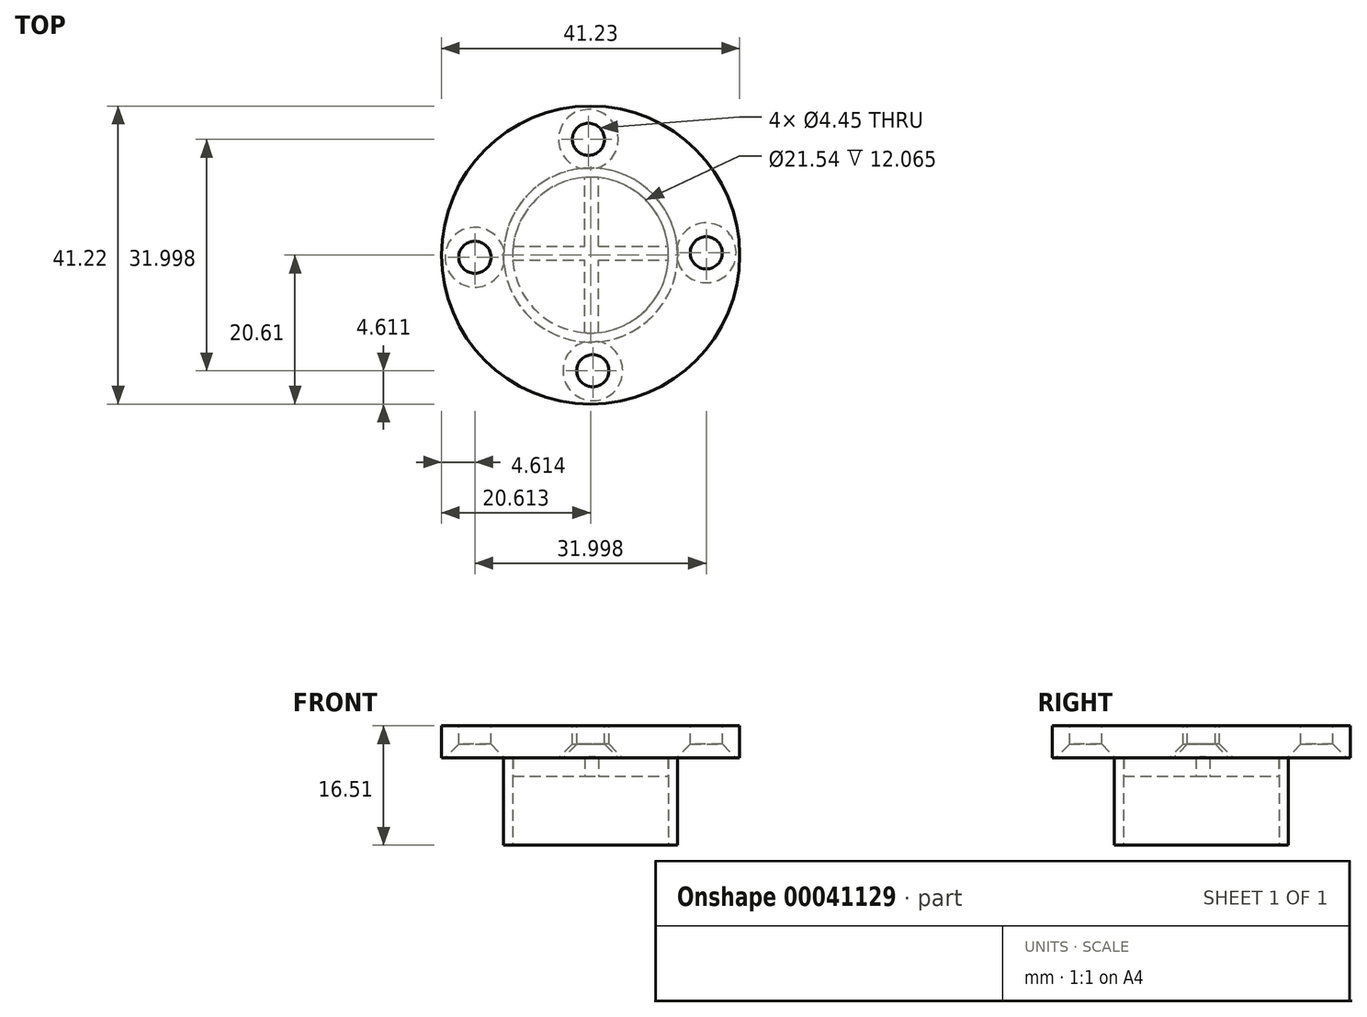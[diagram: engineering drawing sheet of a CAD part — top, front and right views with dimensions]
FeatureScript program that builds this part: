
annotation { "Feature Type Name" : "Feature", "Feature Type Description" : "" }
export const myFeature = defineFeature(function(context is Context, id is Id, definition is map)
    precondition{}
    {
        {
            var Q0;
            Q0=qCreatedBy(makeId("Top.planeOp"),FACE);
            var sketch = newSketch(context, id + "F0", { "sketchPlane" : qUnion([Q0])});
            skCircle(sketch, "E0", {"center": v(-31.53, -46.9) * mm, "radius": 12.04 * mm});
            skCircle(sketch, "E1", {"center": v(-31.53, -46.9) * mm, "radius": 10.77 * mm});
            skSolve(sketch);
        }
        {
            var Q0;
            Q0=makeQuery(id+"F0.imprint","IMPRINT",FACE,{"disambiguationData":[TD([[makeQuery(id+"F0.imprint","IMPRINT",EDGE,{"derivedFrom":sQuery(id+"F0.wireOp",EDGE,"E0")}),1.0]])]});
            extrude(context, id + "F1", {"entities" : qUnion([Q0]), "depth" : 12.06 * mm});
        }
        {
            var Q0;
            Q0=makeQuery(id+"F1.opExtrude","CAP_FACE",FACE,{"disambiguationData":[OSD([sQuery(id+"F0.wireOp",EDGE,"E0"),sQuery(id+"F0.wireOp",EDGE,"E1")])],"isStart":false});
            var sketch = newSketch(context, id + "F2", { "sketchPlane" : qUnion([Q0])});
            skCircle(sketch, "E2", {"center": v(-31.53, -46.9) * mm, "radius": 20.61 * mm});
            skSolve(sketch);
        }
        {
            var Q0;
            Q0 = qSketchRegion(id + "F2", true);
            extrude(context, id + "F3", {"entities" : qUnion([Q0]), "operationType" : NewBodyOperationType.ADD, "depth" : 4.44 * mm});
        }
        {
            var Q0;
            Q0=makeQuery(id+"F3.opExtrude","CAP_FACE",FACE,{"disambiguationData":[OSD([sQuery(id+"F2.wireOp",EDGE,"E2")])],"isStart":false});
            var sketch = newSketch(context, id + "F4", { "sketchPlane" : qUnion([Q0])});
            skCircle(sketch, "E3", {"center": v(-31.83, -30.9) * mm, "radius": 2.22 * mm});
            skPoint(sketch, "E4", {"position": v(-31.53, -46.9) * mm});
            skLineSegment(sketch, "E5", {"start": v(-31.53, -46.9) * mm, "end": v(-31.83, -30.9) * mm});
            skCircle(sketch, "E6", {"center": v(-31.22, -62.89) * mm, "radius": 2.23 * mm});
            skLineSegment(sketch, "E7", {"start": v(-31.53, -46.9) * mm, "end": v(-31.22, -62.89) * mm});
            skCircle(sketch, "E8", {"center": v(-47.53, -47.2) * mm, "radius": 2.23 * mm});
            skCircle(sketch, "E9", {"center": v(-15.53, -46.59) * mm, "radius": 2.23 * mm});
            skLineSegment(sketch, "E10", {"start": v(-31.53, -46.9) * mm, "end": v(-47.53, -47.2) * mm});
            skLineSegment(sketch, "E11", {"start": v(-31.53, -46.9) * mm, "end": v(-15.53, -46.59) * mm});
            skSolve(sketch);
        }
        {
            var Q0;
            Q0 = qSketchRegion(id + "F4", true);
            extrude(context, id + "F5", {"entities" : qUnion([Q0]), "operationType" : NewBodyOperationType.REMOVE, "endBound" : BoundingType.THROUGH_ALL, "oppositeDirection" : true, "depth" : 25.4 * mm});
        }
        {
            var Q0;
            {var subQ0=sQuery(id+"F2.wireOp",EDGE,"E2");Q0=makeQuery(id+"F5.boolean.opBoolean","INTERSECT",EDGE,{"derivedFrom":[makeQuery(id+"F3.boolean.opBoolean","SPLIT",FACE,{"disambiguationData":[TD([makeQuery(id+"F1.opExtrude","SWEPT_FACE",FACE,{"disambiguationData":[OSD([sQuery(id+"F0.wireOp",EDGE,"E0")])]})])],"derivedFrom":makeQuery(id+"F3.opExtrude","CAP_FACE",FACE,{"disambiguationData":[OSD([subQ0])],"isStart":true})}),makeQuery(id+"F5.opExtrude","SWEPT_FACE",FACE,{"disambiguationData":[OSD([sQuery(id+"F4.wireOp",EDGE,"E6")])]})]});}
            var Q1;
            {var subQ0=sQuery(id+"F2.wireOp",EDGE,"E2");Q1=makeQuery(id+"F5.boolean.opBoolean","INTERSECT",EDGE,{"derivedFrom":[makeQuery(id+"F3.boolean.opBoolean","SPLIT",FACE,{"disambiguationData":[TD([makeQuery(id+"F1.opExtrude","SWEPT_FACE",FACE,{"disambiguationData":[OSD([sQuery(id+"F0.wireOp",EDGE,"E0")])]})])],"derivedFrom":makeQuery(id+"F3.opExtrude","CAP_FACE",FACE,{"disambiguationData":[OSD([subQ0])],"isStart":true})}),makeQuery(id+"F5.opExtrude","SWEPT_FACE",FACE,{"disambiguationData":[OSD([sQuery(id+"F4.wireOp",EDGE,"E9")])]})]});}
            var Q2;
            {var subQ0=sQuery(id+"F2.wireOp",EDGE,"E2");Q2=makeQuery(id+"F5.boolean.opBoolean","INTERSECT",EDGE,{"derivedFrom":[makeQuery(id+"F3.boolean.opBoolean","SPLIT",FACE,{"disambiguationData":[TD([makeQuery(id+"F1.opExtrude","SWEPT_FACE",FACE,{"disambiguationData":[OSD([sQuery(id+"F0.wireOp",EDGE,"E0")])]})])],"derivedFrom":makeQuery(id+"F3.opExtrude","CAP_FACE",FACE,{"disambiguationData":[OSD([subQ0])],"isStart":true})}),makeQuery(id+"F5.opExtrude","SWEPT_FACE",FACE,{"disambiguationData":[OSD([sQuery(id+"F4.wireOp",EDGE,"E8")])]})]});}
            var Q3;
            {var subQ0=sQuery(id+"F2.wireOp",EDGE,"E2");Q3=makeQuery(id+"F5.boolean.opBoolean","INTERSECT",EDGE,{"derivedFrom":[makeQuery(id+"F3.boolean.opBoolean","SPLIT",FACE,{"disambiguationData":[TD([makeQuery(id+"F1.opExtrude","SWEPT_FACE",FACE,{"disambiguationData":[OSD([sQuery(id+"F0.wireOp",EDGE,"E0")])]})])],"derivedFrom":makeQuery(id+"F3.opExtrude","CAP_FACE",FACE,{"disambiguationData":[OSD([subQ0])],"isStart":true})}),makeQuery(id+"F5.opExtrude","SWEPT_FACE",FACE,{"disambiguationData":[OSD([sQuery(id+"F4.wireOp",EDGE,"E3")])]})]});}
            chamfer(context, id + "F6", {"entities" : qUnion([Q0, Q1, Q2, Q3]), "width" : 1.9 * mm, "tangentPropagation" : true});
        }
        {
            var Q0;
            {var subQ0=sQuery(id+"F2.wireOp",EDGE,"E2");Q0=makeQuery(id+"F3.boolean.opBoolean","SPLIT",FACE,{"disambiguationData":[TD([makeQuery(id+"F1.opExtrude","SWEPT_FACE",FACE,{"disambiguationData":[OSD([sQuery(id+"F0.wireOp",EDGE,"E0")])]})])],"derivedFrom":makeQuery(id+"F3.opExtrude","CAP_FACE",FACE,{"disambiguationData":[OSD([subQ0])],"isStart":true})});}
            var sketch = newSketch(context, id + "F7", { "sketchPlane" : qUnion([Q0])});
            skLineSegment(sketch, "E12.bottom", {"start": v(-43.14, 47.6) * mm, "end": v(-20.28, 47.6) * mm});
            skLineSegment(sketch, "E12.top", {"start": v(-43.14, 45.7) * mm, "end": v(-20.28, 45.7) * mm});
            skLineSegment(sketch, "E12.left", {"start": v(-43.14, 47.6) * mm, "end": v(-43.14, 45.7) * mm});
            skLineSegment(sketch, "E12.right", {"start": v(-20.28, 47.6) * mm, "end": v(-20.28, 45.7) * mm});
            skLineSegment(sketch, "E13.bottom", {"start": v(-32.36, 58.42) * mm, "end": v(-30.45, 58.42) * mm});
            skLineSegment(sketch, "E13.top", {"start": v(-32.36, 35.56) * mm, "end": v(-30.45, 35.56) * mm});
            skLineSegment(sketch, "E13.left", {"start": v(-32.36, 58.42) * mm, "end": v(-32.36, 35.56) * mm});
            skLineSegment(sketch, "E13.right", {"start": v(-30.45, 58.42) * mm, "end": v(-30.45, 35.56) * mm});
            skSolve(sketch);
        }
        {
            var Q0;
            Q0 = qSketchRegion(id + "F7", true);
            extrude(context, id + "F8", {"entities" : qUnion([Q0]), "operationType" : NewBodyOperationType.ADD, "depth" : 2.54 * mm});
        }
    });
